# Revit family: Haworth_Maari_Stool_AP_PRELIMINARY
name_source: partatom
category: Furniture
units: mm (PartAtom-declared; Revit-internal decimal feet)

## family parameters
Always vertical = Yes
Cut with Voids When Loaded = No
OmniClass Number = 23.40.70.14.64.21
OmniClass Title = Systems Furniture
Room Calculation Point = No
Shared = No
Work Plane-Based = No

## types (6) — shared parameters
Actual Depth = 584 mm
Actual Width = 584 mm
Arm Cap Finish = Haworth _ Polymer _ Undecided
Assembly Code = E2020200
Description = Haworth - Maari - Stool
Manufacturer = Haworth
Model = SEMIGXBX
Revision Number = 2
Size = Verify Final Dim. w/ Haworth
URL = https://www.haworth.com
URL - Product = https://www.haworth.com
Warranty = http://www.haworth.com

## per-type parameters (varying)
| type | Actual Height | Arms Control | Four Legs | Low Back | Sled Base | Standard Back | With Arms | Wood Base |
| Sled Base - Standard Back - No Arms | 1054 mm | No | No | No | Yes | Yes | No | No |
| Four Legs - Standard Back - With Arms | 1054 mm | Yes | Yes | No | No | Yes | Yes | No |
| Wood Leg - Standard Back - No Arms | 1054 mm | No | No | No | No | Yes | No | Yes |
| Sled Base - Low Back - No Arms | 794 mm | No | No | Yes | Yes | No | No | No |
| Four Legs - Standard Back - No Arms | 1054 mm | Yes | Yes | No | No | Yes | Yes | No |
| Wood Leg - Low Back - No Arms | 794 mm | No | No | Yes | No | No | No | Yes |

## geometry (parser evidence)
native form markers: Blend x4, Sweep x6
no freeform markers — native parametric forms only
